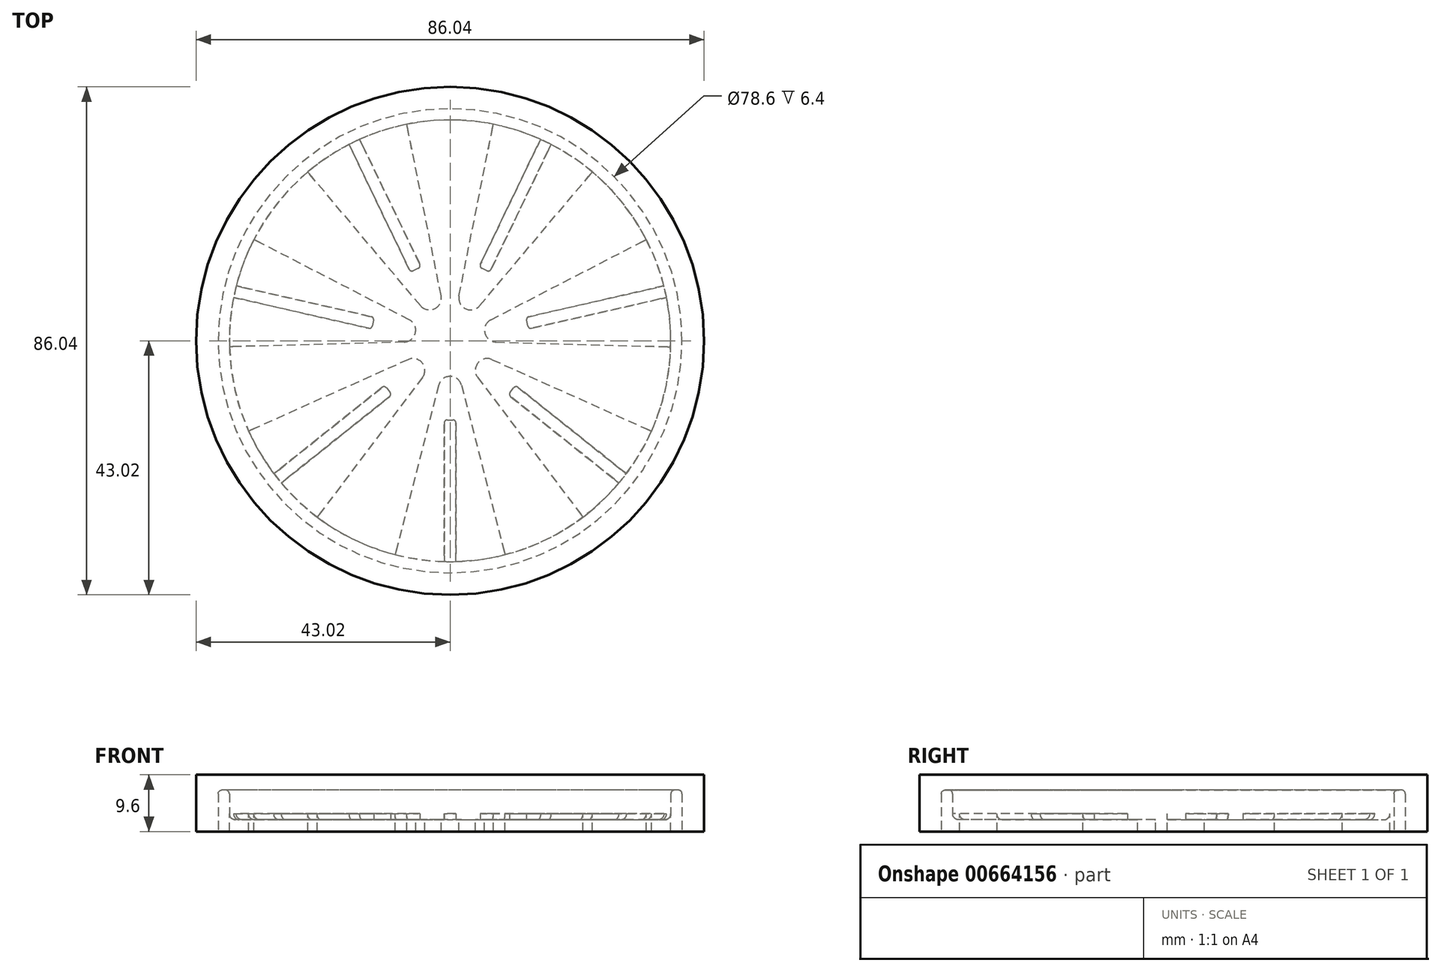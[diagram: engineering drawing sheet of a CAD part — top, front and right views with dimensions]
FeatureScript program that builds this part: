
annotation { "Feature Type Name" : "Feature", "Feature Type Description" : "" }
export const myFeature = defineFeature(function(context is Context, id is Id, definition is map)
    precondition{}
    {
        {
            var Q0;
            Q0=qCreatedBy(makeId("Top.planeOp"),FACE);
            var sketch = newSketch(context, id + "F0", { "sketchPlane" : qUnion([Q0])});
            skCircle(sketch, "E0", {"center": v(0, 0) * mm, "radius": 37.4 * mm});
            skCircle(sketch, "E1", {"center": v(0, 0) * mm, "radius": 39.3 * mm});
            skSolve(sketch);
        }
        {
            var Q0;
            Q0=makeQuery(id+"F0.imprint","IMPRINT",FACE,{"disambiguationData":[TD([[makeQuery(id+"F0.imprint","IMPRINT",EDGE,{"derivedFrom":sQuery(id+"F0.wireOp",EDGE,"E0")}),-1.0]])]});
            extrude(context, id + "F1", {"entities" : qUnion([Q0]), "depth" : 7 * mm, "offsetDistance" : 25 * mm});
        }
        {
            var Q0;
            Q0=qCreatedBy(makeId("Top.planeOp"),FACE);
            var sketch = newSketch(context, id + "F2", { "sketchPlane" : qUnion([Q0])});
            skCircle(sketch, "E2", {"center": v(0, 0) * mm, "radius": 37.45 * mm});
            skSolve(sketch);
        }
        {
            var Q0;
            Q0=makeQuery(id+"F2.imprint","IMPRINT",FACE,{"disambiguationData":[TD([[makeQuery(id+"F2.imprint","IMPRINT",EDGE,{"derivedFrom":sQuery(id+"F2.wireOp",EDGE,"E2")}),1.0]])]});
            extrude(context, id + "F3", {"entities" : qUnion([Q0]), "operationType" : NewBodyOperationType.ADD, "depth" : 2 * mm, "offsetDistance" : 25 * mm});
        }
        {
            var Q0;
            Q0=makeQuery(id+"F3.opExtrude","CAP_FACE",FACE,{"disambiguationData":[OSD([sQuery(id+"F2.wireOp",EDGE,"E2")])],"isStart":false});
            var sketch = newSketch(context, id + "F4", { "sketchPlane" : qUnion([Q0])});
            skCircle(sketch, "E3", {"center": v(0, 0) * mm, "radius": 38.06 * mm});
            skLineSegment(sketch, "E4", {"start": v(1.94, -7.53) * mm, "end": v(9.48, -36.86) * mm});
            skLineSegment(sketch, "E5.MirrorCS", {"start": v(-1.94, -7.53) * mm, "end": v(-9.48, -36.86) * mm});
            skPoint(sketch, "E6.orphan", {"position": v(-11.58, -45.02) * mm});
            skPoint(sketch, "E7.orphan", {"position": v(11.58, -45.02) * mm});
            skArc(sketch, "E8.filletArc", {"start": v(1.94, -7.53) * mm, "mid": v(0, -6.03) * mm, "end": v(-1.94, -7.53) * mm});
            skLineSegment(sketch, "E9.1.0", {"start": v(4.68, -6.21) * mm, "end": v(22.91, -30.4) * mm});
            skLineSegment(sketch, "E9.1.1", {"start": v(7.1, -3.18) * mm, "end": v(34.73, -15.57) * mm});
            skArc(sketch, "E9.1.2", {"start": v(7.1, -3.18) * mm, "mid": v(4.71, -3.76) * mm, "end": v(4.68, -6.21) * mm});
            skLineSegment(sketch, "E9.2.0", {"start": v(7.77, -0.21) * mm, "end": v(38.05, -1.04) * mm});
            skLineSegment(sketch, "E9.2.1", {"start": v(6.91, 3.56) * mm, "end": v(33.83, 17.45) * mm});
            skArc(sketch, "E9.2.2", {"start": v(6.91, 3.56) * mm, "mid": v(5.88, 1.34) * mm, "end": v(7.77, -0.21) * mm});
            skLineSegment(sketch, "E9.3.0", {"start": v(5.01, 5.95) * mm, "end": v(24.54, 29.1) * mm});
            skLineSegment(sketch, "E9.3.1", {"start": v(1.52, 7.63) * mm, "end": v(7.45, 37.33) * mm});
            skArc(sketch, "E9.3.2", {"start": v(1.52, 7.63) * mm, "mid": v(2.62, 5.43) * mm, "end": v(5.01, 5.95) * mm});
            skLineSegment(sketch, "E9.4.0", {"start": v(-1.52, 7.63) * mm, "end": v(-7.45, 37.33) * mm});
            skLineSegment(sketch, "E9.4.1", {"start": v(-5.01, 5.95) * mm, "end": v(-24.54, 29.1) * mm});
            skArc(sketch, "E9.4.2", {"start": v(-5.01, 5.95) * mm, "mid": v(-2.62, 5.43) * mm, "end": v(-1.52, 7.63) * mm});
            skLineSegment(sketch, "E9.5.0", {"start": v(-6.91, 3.56) * mm, "end": v(-33.83, 17.45) * mm});
            skLineSegment(sketch, "E9.5.1", {"start": v(-7.77, -0.21) * mm, "end": v(-38.05, -1.04) * mm});
            skArc(sketch, "E9.5.2", {"start": v(-7.77, -0.21) * mm, "mid": v(-5.88, 1.34) * mm, "end": v(-6.91, 3.56) * mm});
            skLineSegment(sketch, "E10.2.6.0", {"start": v(-7.1, -3.18) * mm, "end": v(-34.73, -15.57) * mm});
            skLineSegment(sketch, "E10.3.6.0", {"start": v(-4.68, -6.21) * mm, "end": v(-22.91, -30.4) * mm});
            skArc(sketch, "E10.6.6.0", {"start": v(-4.68, -6.21) * mm, "mid": v(-4.71, -3.76) * mm, "end": v(-7.1, -3.18) * mm});
            skSolve(sketch);
        }
        {
            var Q0;
            {var subQ24=sQuery(id+"F4.wireOp",EDGE,"E8.filletArc");Q0=makeQuery(id+"F4.imprint","IMPRINT",FACE,{"disambiguationData":[TD([[makeQuery(id+"F4.imprint","IMPRINT",EDGE,{"derivedFrom":subQ24}),-1.0]])]});}
            extrude(context, id + "F5", {"entities" : qUnion([Q0]), "operationType" : NewBodyOperationType.REMOVE, "oppositeDirection" : true, "depth" : 25 * mm, "offsetDistance" : 25 * mm});
        }
        {
            var Q0;
            Q0=makeQuery(id+"F3.boolean.opBoolean","MERGE",FACE,{"derivedFrom":[makeQuery(id+"F1.opExtrude","CAP_FACE",FACE,{"disambiguationData":[OSD([sQuery(id+"F0.wireOp",EDGE,"E0"),sQuery(id+"F0.wireOp",EDGE,"E1")])],"isStart":true}),makeQuery(id+"F3.opExtrude","CAP_FACE",FACE,{"disambiguationData":[OSD([sQuery(id+"F2.wireOp",EDGE,"E2")])],"isStart":true})]});
            var sketch = newSketch(context, id + "F6", { "sketchPlane" : qUnion([Q0])});
            skLineSegment(sketch, "E11", {"start": v(1, 38.32) * mm, "end": v(1, 13.9) * mm});
            skLineSegment(sketch, "E12", {"start": v(0.5, 13.4) * mm, "end": v(-0.5, 13.4) * mm});
            skLineSegment(sketch, "E13", {"start": v(-1, 13.9) * mm, "end": v(-1, 38.32) * mm});
            skPoint(sketch, "E14.visualSharp", {"position": v(-1, 13.4) * mm});
            skArc(sketch, "E14.filletArc", {"start": v(-1, 13.9) * mm, "mid": v(-0.85, 13.55) * mm, "end": v(-0.5, 13.4) * mm});
            skPoint(sketch, "E15.visualSharp", {"position": v(1, 13.4) * mm});
            skArc(sketch, "E15.filletArc", {"start": v(0.5, 13.4) * mm, "mid": v(0.85, 13.55) * mm, "end": v(1, 13.9) * mm});
            skLineSegment(sketch, "E16", {"start": v(-0.5, 38.82) * mm, "end": v(0.5, 38.82) * mm});
            skPoint(sketch, "E17.visualSharp", {"position": v(-1, 38.82) * mm});
            skArc(sketch, "E17.filletArc", {"start": v(-0.5, 38.82) * mm, "mid": v(-0.85, 38.68) * mm, "end": v(-1, 38.32) * mm});
            skPoint(sketch, "E18.visualSharp", {"position": v(1, 38.82) * mm});
            skArc(sketch, "E18.filletArc", {"start": v(1, 38.32) * mm, "mid": v(0.85, 38.68) * mm, "end": v(0.5, 38.82) * mm});
            skPoint(sketch, "E19.1.0", {"position": v(-11.1, 7.58) * mm});
            skPoint(sketch, "E19.1.1", {"position": v(-29.73, 24.99) * mm});
            skLineSegment(sketch, "E19.1.2", {"start": v(-11.5, 7.89) * mm, "end": v(-30.59, 23.11) * mm});
            skPoint(sketch, "E19.1.3", {"position": v(-30.98, 23.42) * mm});
            skLineSegment(sketch, "E19.1.4", {"start": v(-29.34, 24.68) * mm, "end": v(-10.25, 9.45) * mm});
            skPoint(sketch, "E19.1.5", {"position": v(-9.86, 9.14) * mm});
            skArc(sketch, "E19.1.6", {"start": v(-10.17, 8.75) * mm, "mid": v(-10.07, 9.12) * mm, "end": v(-10.25, 9.45) * mm});
            skArc(sketch, "E19.1.7", {"start": v(-30.66, 23.81) * mm, "mid": v(-30.77, 23.45) * mm, "end": v(-30.59, 23.11) * mm});
            skArc(sketch, "E19.1.8", {"start": v(-11.5, 7.89) * mm, "mid": v(-11.13, 7.78) * mm, "end": v(-10.8, 7.97) * mm});
            skLineSegment(sketch, "E19.1.9", {"start": v(-10.17, 8.75) * mm, "end": v(-10.8, 7.97) * mm});
            skLineSegment(sketch, "E19.1.10", {"start": v(-30.66, 23.81) * mm, "end": v(-30.04, 24.6) * mm});
            skArc(sketch, "E19.1.11", {"start": v(-29.34, 24.68) * mm, "mid": v(-29.7, 24.78) * mm, "end": v(-30.04, 24.6) * mm});
            skPoint(sketch, "E19.2.0", {"position": v(-12.85, -3.96) * mm});
            skPoint(sketch, "E19.2.1", {"position": v(-38.07, -7.66) * mm});
            skLineSegment(sketch, "E19.2.2", {"start": v(-13.34, -4.07) * mm, "end": v(-37.14, -9.5) * mm});
            skPoint(sketch, "E19.2.3", {"position": v(-37.63, -9.61) * mm});
            skLineSegment(sketch, "E19.2.4", {"start": v(-37.58, -7.55) * mm, "end": v(-13.78, -2.12) * mm});
            skPoint(sketch, "E19.2.5", {"position": v(-13.3, -2) * mm});
            skArc(sketch, "E19.2.6", {"start": v(-13.18, -2.5) * mm, "mid": v(-13.4, -2.18) * mm, "end": v(-13.78, -2.12) * mm});
            skArc(sketch, "E19.2.7", {"start": v(-37.74, -9.13) * mm, "mid": v(-37.52, -9.44) * mm, "end": v(-37.14, -9.5) * mm});
            skArc(sketch, "E19.2.8", {"start": v(-13.34, -4.07) * mm, "mid": v(-13.03, -3.85) * mm, "end": v(-12.96, -3.47) * mm});
            skLineSegment(sketch, "E19.2.9", {"start": v(-13.18, -2.5) * mm, "end": v(-12.96, -3.47) * mm});
            skLineSegment(sketch, "E19.2.10", {"start": v(-37.74, -9.13) * mm, "end": v(-37.96, -8.15) * mm});
            skArc(sketch, "E19.2.11", {"start": v(-37.58, -7.55) * mm, "mid": v(-37.9, -7.77) * mm, "end": v(-37.96, -8.15) * mm});
            skPoint(sketch, "E19.3.0", {"position": v(-4.92, -12.51) * mm});
            skPoint(sketch, "E19.3.1", {"position": v(-17.75, -34.54) * mm});
            skLineSegment(sketch, "E19.3.2", {"start": v(-5.13, -12.96) * mm, "end": v(-15.73, -34.96) * mm});
            skPoint(sketch, "E19.3.3", {"position": v(-15.94, -35.41) * mm});
            skLineSegment(sketch, "E19.3.4", {"start": v(-17.53, -34.1) * mm, "end": v(-6.94, -12.1) * mm});
            skPoint(sketch, "E19.3.5", {"position": v(-6.72, -11.65) * mm});
            skArc(sketch, "E19.3.6", {"start": v(-6.27, -11.86) * mm, "mid": v(-6.65, -11.84) * mm, "end": v(-6.94, -12.1) * mm});
            skArc(sketch, "E19.3.7", {"start": v(-16.4, -35.2) * mm, "mid": v(-16.01, -35.22) * mm, "end": v(-15.73, -34.96) * mm});
            skArc(sketch, "E19.3.8", {"start": v(-5.13, -12.96) * mm, "mid": v(-5.11, -12.58) * mm, "end": v(-5.37, -12.3) * mm});
            skLineSegment(sketch, "E19.3.9", {"start": v(-6.27, -11.86) * mm, "end": v(-5.37, -12.3) * mm});
            skLineSegment(sketch, "E19.3.10", {"start": v(-16.4, -35.2) * mm, "end": v(-17.3, -34.76) * mm});
            skArc(sketch, "E19.3.11", {"start": v(-17.53, -34.1) * mm, "mid": v(-17.55, -34.48) * mm, "end": v(-17.3, -34.76) * mm});
            skPoint(sketch, "E19.4.0", {"position": v(6.72, -11.65) * mm});
            skPoint(sketch, "E19.4.1", {"position": v(15.94, -35.41) * mm});
            skLineSegment(sketch, "E19.4.2", {"start": v(6.94, -12.1) * mm, "end": v(17.53, -34.1) * mm});
            skPoint(sketch, "E19.4.3", {"position": v(17.75, -34.54) * mm});
            skLineSegment(sketch, "E19.4.4", {"start": v(15.73, -34.96) * mm, "end": v(5.13, -12.96) * mm});
            skPoint(sketch, "E19.4.5", {"position": v(4.92, -12.51) * mm});
            skArc(sketch, "E19.4.6", {"start": v(5.37, -12.3) * mm, "mid": v(5.11, -12.58) * mm, "end": v(5.13, -12.96) * mm});
            skArc(sketch, "E19.4.7", {"start": v(17.3, -34.76) * mm, "mid": v(17.55, -34.48) * mm, "end": v(17.53, -34.1) * mm});
            skArc(sketch, "E19.4.8", {"start": v(6.94, -12.1) * mm, "mid": v(6.65, -11.84) * mm, "end": v(6.27, -11.86) * mm});
            skLineSegment(sketch, "E19.4.9", {"start": v(5.37, -12.3) * mm, "end": v(6.27, -11.86) * mm});
            skLineSegment(sketch, "E19.4.10", {"start": v(17.3, -34.76) * mm, "end": v(16.4, -35.2) * mm});
            skArc(sketch, "E19.4.11", {"start": v(15.73, -34.96) * mm, "mid": v(16.01, -35.22) * mm, "end": v(16.4, -35.2) * mm});
            skPoint(sketch, "E19.5.0", {"position": v(13.3, -2) * mm});
            skPoint(sketch, "E19.5.1", {"position": v(37.63, -9.61) * mm});
            skLineSegment(sketch, "E19.5.2", {"start": v(13.78, -2.12) * mm, "end": v(37.58, -7.55) * mm});
            skPoint(sketch, "E19.5.3", {"position": v(38.07, -7.66) * mm});
            skLineSegment(sketch, "E19.5.4", {"start": v(37.14, -9.5) * mm, "end": v(13.34, -4.07) * mm});
            skPoint(sketch, "E19.5.5", {"position": v(12.85, -3.96) * mm});
            skArc(sketch, "E19.5.6", {"start": v(12.96, -3.47) * mm, "mid": v(13.03, -3.85) * mm, "end": v(13.34, -4.07) * mm});
            skArc(sketch, "E19.5.7", {"start": v(37.96, -8.15) * mm, "mid": v(37.9, -7.77) * mm, "end": v(37.58, -7.55) * mm});
            skArc(sketch, "E19.5.8", {"start": v(13.78, -2.12) * mm, "mid": v(13.4, -2.18) * mm, "end": v(13.18, -2.5) * mm});
            skLineSegment(sketch, "E19.5.9", {"start": v(12.96, -3.47) * mm, "end": v(13.18, -2.5) * mm});
            skLineSegment(sketch, "E19.5.10", {"start": v(37.96, -8.15) * mm, "end": v(37.74, -9.13) * mm});
            skArc(sketch, "E19.5.11", {"start": v(37.14, -9.5) * mm, "mid": v(37.52, -9.44) * mm, "end": v(37.74, -9.13) * mm});
            skPoint(sketch, "E19.6.0", {"position": v(9.86, 9.14) * mm});
            skPoint(sketch, "E19.6.1", {"position": v(30.98, 23.42) * mm});
            skLineSegment(sketch, "E19.6.2", {"start": v(10.25, 9.45) * mm, "end": v(29.34, 24.68) * mm});
            skPoint(sketch, "E19.6.3", {"position": v(29.73, 24.99) * mm});
            skLineSegment(sketch, "E19.6.4", {"start": v(30.59, 23.11) * mm, "end": v(11.5, 7.89) * mm});
            skPoint(sketch, "E19.6.5", {"position": v(11.1, 7.58) * mm});
            skArc(sketch, "E19.6.6", {"start": v(10.8, 7.97) * mm, "mid": v(11.13, 7.78) * mm, "end": v(11.5, 7.89) * mm});
            skArc(sketch, "E19.6.7", {"start": v(30.04, 24.6) * mm, "mid": v(29.7, 24.78) * mm, "end": v(29.34, 24.68) * mm});
            skArc(sketch, "E19.6.8", {"start": v(10.25, 9.45) * mm, "mid": v(10.07, 9.12) * mm, "end": v(10.17, 8.75) * mm});
            skLineSegment(sketch, "E19.6.9", {"start": v(10.8, 7.97) * mm, "end": v(10.17, 8.75) * mm});
            skLineSegment(sketch, "E19.6.10", {"start": v(30.04, 24.6) * mm, "end": v(30.66, 23.81) * mm});
            skArc(sketch, "E19.6.11", {"start": v(30.59, 23.11) * mm, "mid": v(30.77, 23.45) * mm, "end": v(30.66, 23.81) * mm});
            skPoint(sketch, "E19.center", {"position": v(0, 0) * mm});
            skSolve(sketch);
        }
        {
            var Q0;
            Q0=qSketchRegion(id+"F6",true);
            extrude(context, id + "F7", {"entities" : qUnion([Q0]), "operationType" : NewBodyOperationType.ADD, "depth" : -3 * mm, "offsetDistance" : 25 * mm});
        }
        {
            var Q0;
            {var subQ0=sQuery(id+"F2.wireOp",EDGE,"E2");var subQ1=makeQuery(id+"F3.opExtrude","CAP_FACE",FACE,{"disambiguationData":[OSD([subQ0])],"isStart":false});var subQ2=sQuery(id+"F0.wireOp",EDGE,"E0");var subQ3=makeQuery(id+"F1.opExtrude","SWEPT_FACE",FACE,{"disambiguationData":[OSD([subQ2])]});var subQ4=makeQuery(id+"F3.boolean.opBoolean","INTERSECT",EDGE,{"derivedFrom":[subQ3,subQ1]});var subQ5=sQuery(id+"F4.wireOp",EDGE,"E10.2.6.0");var subQ8=makeQuery(id+"F5.opExtrude","SWEPT_FACE",FACE,{"disambiguationData":[OSD([subQ5])]});Q0=makeQuery(id+"F7.boolean.opBoolean","SPLIT",EDGE,{"disambiguationData":[TD([makeQuery(id+"F5.boolean.opBoolean","COPY",FACE,{"derivedFrom":subQ8})])],"derivedFrom":makeQuery(id+"F5.boolean.opBoolean","SPLIT",EDGE,{"disambiguationData":[TD([subQ8])],"derivedFrom":subQ4})});}
            var Q1;
            {var subQ0=sQuery(id+"F2.wireOp",EDGE,"E2");var subQ1=makeQuery(id+"F3.opExtrude","CAP_FACE",FACE,{"disambiguationData":[OSD([subQ0])],"isStart":false});var subQ2=sQuery(id+"F0.wireOp",EDGE,"E0");var subQ3=makeQuery(id+"F1.opExtrude","SWEPT_FACE",FACE,{"disambiguationData":[OSD([subQ2])]});var subQ4=makeQuery(id+"F3.boolean.opBoolean","INTERSECT",EDGE,{"derivedFrom":[subQ3,subQ1]});var subQ6=sQuery(id+"F4.wireOp",EDGE,"E5.MirrorCS");var subQ7=makeQuery(id+"F5.opExtrude","SWEPT_FACE",FACE,{"disambiguationData":[OSD([subQ6])]});var subQ12=sQuery(id+"F4.wireOp",EDGE,"E4");Q1=makeQuery(id+"F7.boolean.opBoolean","SPLIT",EDGE,{"disambiguationData":[TD([makeQuery(id+"F5.boolean.opBoolean","COPY",FACE,{"derivedFrom":subQ7})])],"derivedFrom":makeQuery(id+"F5.boolean.opBoolean","SPLIT",EDGE,{"disambiguationData":[TD([makeQuery(id+"F5.opExtrude","SWEPT_FACE",FACE,{"disambiguationData":[OSD([subQ12])]})])],"derivedFrom":subQ4})});}
            var Q2;
            {var subQ0=sQuery(id+"F2.wireOp",EDGE,"E2");var subQ1=makeQuery(id+"F3.opExtrude","CAP_FACE",FACE,{"disambiguationData":[OSD([subQ0])],"isStart":false});var subQ2=sQuery(id+"F0.wireOp",EDGE,"E0");var subQ3=makeQuery(id+"F1.opExtrude","SWEPT_FACE",FACE,{"disambiguationData":[OSD([subQ2])]});var subQ4=makeQuery(id+"F3.boolean.opBoolean","INTERSECT",EDGE,{"derivedFrom":[subQ3,subQ1]});var subQ9=sQuery(id+"F4.wireOp",EDGE,"E4");var subQ10=makeQuery(id+"F5.opExtrude","SWEPT_FACE",FACE,{"disambiguationData":[OSD([subQ9])]});Q2=makeQuery(id+"F7.boolean.opBoolean","SPLIT",EDGE,{"disambiguationData":[TD([makeQuery(id+"F5.boolean.opBoolean","COPY",FACE,{"derivedFrom":subQ10})])],"derivedFrom":makeQuery(id+"F5.boolean.opBoolean","SPLIT",EDGE,{"disambiguationData":[TD([subQ10])],"derivedFrom":subQ4})});}
            var Q3;
            {var subQ0=sQuery(id+"F2.wireOp",EDGE,"E2");var subQ1=makeQuery(id+"F3.opExtrude","CAP_FACE",FACE,{"disambiguationData":[OSD([subQ0])],"isStart":false});var subQ2=sQuery(id+"F0.wireOp",EDGE,"E0");var subQ3=makeQuery(id+"F1.opExtrude","SWEPT_FACE",FACE,{"disambiguationData":[OSD([subQ2])]});var subQ4=makeQuery(id+"F3.boolean.opBoolean","INTERSECT",EDGE,{"derivedFrom":[subQ3,subQ1]});var subQ5=sQuery(id+"F4.wireOp",EDGE,"E10.2.6.0");var subQ7=sQuery(id+"F4.wireOp",EDGE,"E10.3.6.0");var subQ8=makeQuery(id+"F5.opExtrude","SWEPT_FACE",FACE,{"disambiguationData":[OSD([subQ7])]});Q3=makeQuery(id+"F7.boolean.opBoolean","SPLIT",EDGE,{"disambiguationData":[TD([makeQuery(id+"F5.boolean.opBoolean","COPY",FACE,{"derivedFrom":subQ8})])],"derivedFrom":makeQuery(id+"F5.boolean.opBoolean","SPLIT",EDGE,{"disambiguationData":[TD([makeQuery(id+"F5.opExtrude","SWEPT_FACE",FACE,{"disambiguationData":[OSD([subQ5])]})])],"derivedFrom":subQ4})});}
            var Q4;
            {var subQ0=sQuery(id+"F2.wireOp",EDGE,"E2");var subQ1=makeQuery(id+"F3.opExtrude","CAP_FACE",FACE,{"disambiguationData":[OSD([subQ0])],"isStart":false});var subQ2=sQuery(id+"F0.wireOp",EDGE,"E0");var subQ3=makeQuery(id+"F1.opExtrude","SWEPT_FACE",FACE,{"disambiguationData":[OSD([subQ2])]});var subQ4=makeQuery(id+"F3.boolean.opBoolean","INTERSECT",EDGE,{"derivedFrom":[subQ3,subQ1]});var subQ11=sQuery(id+"F4.wireOp",EDGE,"E9.1.0");var subQ12=makeQuery(id+"F5.opExtrude","SWEPT_FACE",FACE,{"disambiguationData":[OSD([subQ11])]});Q4=makeQuery(id+"F7.boolean.opBoolean","SPLIT",EDGE,{"disambiguationData":[TD([makeQuery(id+"F5.boolean.opBoolean","COPY",FACE,{"derivedFrom":subQ12})])],"derivedFrom":makeQuery(id+"F5.boolean.opBoolean","SPLIT",EDGE,{"disambiguationData":[TD([subQ12])],"derivedFrom":subQ4})});}
            var Q5;
            {var subQ0=sQuery(id+"F4.wireOp",EDGE,"E9.1.1");var subQ1=makeQuery(id+"F5.opExtrude","SWEPT_FACE",FACE,{"disambiguationData":[OSD([subQ0])]});var subQ2=sQuery(id+"F2.wireOp",EDGE,"E2");var subQ3=makeQuery(id+"F3.opExtrude","CAP_FACE",FACE,{"disambiguationData":[OSD([subQ2])],"isStart":false});var subQ4=sQuery(id+"F0.wireOp",EDGE,"E0");var subQ5=makeQuery(id+"F1.opExtrude","SWEPT_FACE",FACE,{"disambiguationData":[OSD([subQ4])]});var subQ6=makeQuery(id+"F3.boolean.opBoolean","INTERSECT",EDGE,{"derivedFrom":[subQ5,subQ3]});var subQ12=sQuery(id+"F4.wireOp",EDGE,"E9.1.0");Q5=makeQuery(id+"F7.boolean.opBoolean","SPLIT",EDGE,{"disambiguationData":[TD([makeQuery(id+"F5.boolean.opBoolean","COPY",FACE,{"derivedFrom":subQ1})])],"derivedFrom":makeQuery(id+"F5.boolean.opBoolean","SPLIT",EDGE,{"disambiguationData":[TD([makeQuery(id+"F5.opExtrude","SWEPT_FACE",FACE,{"disambiguationData":[OSD([subQ12])]})])],"derivedFrom":subQ6})});}
            var Q6;
            {var subQ0=sQuery(id+"F4.wireOp",EDGE,"E9.5.0");var subQ1=makeQuery(id+"F5.opExtrude","SWEPT_FACE",FACE,{"disambiguationData":[OSD([subQ0])]});var subQ2=sQuery(id+"F2.wireOp",EDGE,"E2");var subQ3=makeQuery(id+"F3.opExtrude","CAP_FACE",FACE,{"disambiguationData":[OSD([subQ2])],"isStart":false});var subQ4=sQuery(id+"F0.wireOp",EDGE,"E0");var subQ5=makeQuery(id+"F1.opExtrude","SWEPT_FACE",FACE,{"disambiguationData":[OSD([subQ4])]});var subQ6=makeQuery(id+"F3.boolean.opBoolean","INTERSECT",EDGE,{"derivedFrom":[subQ5,subQ3]});Q6=makeQuery(id+"F7.boolean.opBoolean","SPLIT",EDGE,{"disambiguationData":[TD([makeQuery(id+"F5.boolean.opBoolean","COPY",FACE,{"derivedFrom":subQ1})])],"derivedFrom":makeQuery(id+"F5.boolean.opBoolean","SPLIT",EDGE,{"disambiguationData":[TD([subQ1])],"derivedFrom":subQ6})});}
            var Q7;
            {var subQ0=sQuery(id+"F4.wireOp",EDGE,"E9.4.1");var subQ1=makeQuery(id+"F5.opExtrude","SWEPT_FACE",FACE,{"disambiguationData":[OSD([subQ0])]});var subQ2=sQuery(id+"F2.wireOp",EDGE,"E2");var subQ3=makeQuery(id+"F3.opExtrude","CAP_FACE",FACE,{"disambiguationData":[OSD([subQ2])],"isStart":false});var subQ4=sQuery(id+"F0.wireOp",EDGE,"E0");var subQ5=makeQuery(id+"F1.opExtrude","SWEPT_FACE",FACE,{"disambiguationData":[OSD([subQ4])]});var subQ6=makeQuery(id+"F3.boolean.opBoolean","INTERSECT",EDGE,{"derivedFrom":[subQ5,subQ3]});var subQ12=sQuery(id+"F4.wireOp",EDGE,"E9.4.0");Q7=makeQuery(id+"F7.boolean.opBoolean","SPLIT",EDGE,{"disambiguationData":[TD([makeQuery(id+"F5.boolean.opBoolean","COPY",FACE,{"derivedFrom":subQ1})])],"derivedFrom":makeQuery(id+"F5.boolean.opBoolean","SPLIT",EDGE,{"disambiguationData":[TD([makeQuery(id+"F5.opExtrude","SWEPT_FACE",FACE,{"disambiguationData":[OSD([subQ12])]})])],"derivedFrom":subQ6})});}
            var Q8;
            {var subQ0=sQuery(id+"F2.wireOp",EDGE,"E2");var subQ1=makeQuery(id+"F3.opExtrude","CAP_FACE",FACE,{"disambiguationData":[OSD([subQ0])],"isStart":false});var subQ2=sQuery(id+"F0.wireOp",EDGE,"E0");var subQ3=makeQuery(id+"F1.opExtrude","SWEPT_FACE",FACE,{"disambiguationData":[OSD([subQ2])]});var subQ4=makeQuery(id+"F3.boolean.opBoolean","INTERSECT",EDGE,{"derivedFrom":[subQ3,subQ1]});var subQ6=sQuery(id+"F4.wireOp",EDGE,"E9.4.0");var subQ7=makeQuery(id+"F5.opExtrude","SWEPT_FACE",FACE,{"disambiguationData":[OSD([subQ6])]});Q8=makeQuery(id+"F7.boolean.opBoolean","SPLIT",EDGE,{"disambiguationData":[TD([makeQuery(id+"F5.boolean.opBoolean","COPY",FACE,{"derivedFrom":subQ7})])],"derivedFrom":makeQuery(id+"F5.boolean.opBoolean","SPLIT",EDGE,{"disambiguationData":[TD([subQ7])],"derivedFrom":subQ4})});}
            var Q9;
            {var subQ0=sQuery(id+"F4.wireOp",EDGE,"E9.5.1");var subQ1=makeQuery(id+"F5.opExtrude","SWEPT_FACE",FACE,{"disambiguationData":[OSD([subQ0])]});var subQ2=sQuery(id+"F2.wireOp",EDGE,"E2");var subQ3=makeQuery(id+"F3.opExtrude","CAP_FACE",FACE,{"disambiguationData":[OSD([subQ2])],"isStart":false});var subQ4=sQuery(id+"F0.wireOp",EDGE,"E0");var subQ5=makeQuery(id+"F1.opExtrude","SWEPT_FACE",FACE,{"disambiguationData":[OSD([subQ4])]});var subQ6=makeQuery(id+"F3.boolean.opBoolean","INTERSECT",EDGE,{"derivedFrom":[subQ5,subQ3]});var subQ9=sQuery(id+"F4.wireOp",EDGE,"E9.5.0");Q9=makeQuery(id+"F7.boolean.opBoolean","SPLIT",EDGE,{"disambiguationData":[TD([makeQuery(id+"F5.boolean.opBoolean","COPY",FACE,{"derivedFrom":subQ1})])],"derivedFrom":makeQuery(id+"F5.boolean.opBoolean","SPLIT",EDGE,{"disambiguationData":[TD([makeQuery(id+"F5.opExtrude","SWEPT_FACE",FACE,{"disambiguationData":[OSD([subQ9])]})])],"derivedFrom":subQ6})});}
            var Q10;
            {var subQ0=sQuery(id+"F4.wireOp",EDGE,"E9.2.0");var subQ1=makeQuery(id+"F5.opExtrude","SWEPT_FACE",FACE,{"disambiguationData":[OSD([subQ0])]});var subQ2=sQuery(id+"F2.wireOp",EDGE,"E2");var subQ3=makeQuery(id+"F3.opExtrude","CAP_FACE",FACE,{"disambiguationData":[OSD([subQ2])],"isStart":false});var subQ4=sQuery(id+"F0.wireOp",EDGE,"E0");var subQ5=makeQuery(id+"F1.opExtrude","SWEPT_FACE",FACE,{"disambiguationData":[OSD([subQ4])]});var subQ6=makeQuery(id+"F3.boolean.opBoolean","INTERSECT",EDGE,{"derivedFrom":[subQ5,subQ3]});Q10=makeQuery(id+"F7.boolean.opBoolean","SPLIT",EDGE,{"disambiguationData":[TD([makeQuery(id+"F5.boolean.opBoolean","COPY",FACE,{"derivedFrom":subQ1})])],"derivedFrom":makeQuery(id+"F5.boolean.opBoolean","SPLIT",EDGE,{"disambiguationData":[TD([subQ1])],"derivedFrom":subQ6})});}
            var Q11;
            {var subQ0=sQuery(id+"F2.wireOp",EDGE,"E2");var subQ1=makeQuery(id+"F3.opExtrude","CAP_FACE",FACE,{"disambiguationData":[OSD([subQ0])],"isStart":false});var subQ2=sQuery(id+"F0.wireOp",EDGE,"E0");var subQ3=makeQuery(id+"F1.opExtrude","SWEPT_FACE",FACE,{"disambiguationData":[OSD([subQ2])]});var subQ4=makeQuery(id+"F3.boolean.opBoolean","INTERSECT",EDGE,{"derivedFrom":[subQ3,subQ1]});var subQ7=sQuery(id+"F4.wireOp",EDGE,"E9.2.1");var subQ9=sQuery(id+"F4.wireOp",EDGE,"E9.2.0");var subQ12=makeQuery(id+"F5.opExtrude","SWEPT_FACE",FACE,{"disambiguationData":[OSD([subQ7])]});Q11=makeQuery(id+"F7.boolean.opBoolean","SPLIT",EDGE,{"disambiguationData":[TD([makeQuery(id+"F5.boolean.opBoolean","COPY",FACE,{"derivedFrom":subQ12})])],"derivedFrom":makeQuery(id+"F5.boolean.opBoolean","SPLIT",EDGE,{"disambiguationData":[TD([makeQuery(id+"F5.opExtrude","SWEPT_FACE",FACE,{"disambiguationData":[OSD([subQ9])]})])],"derivedFrom":subQ4})});}
            var Q12;
            {var subQ0=sQuery(id+"F2.wireOp",EDGE,"E2");var subQ1=makeQuery(id+"F3.opExtrude","CAP_FACE",FACE,{"disambiguationData":[OSD([subQ0])],"isStart":false});var subQ2=sQuery(id+"F0.wireOp",EDGE,"E0");var subQ3=makeQuery(id+"F1.opExtrude","SWEPT_FACE",FACE,{"disambiguationData":[OSD([subQ2])]});var subQ4=makeQuery(id+"F3.boolean.opBoolean","INTERSECT",EDGE,{"derivedFrom":[subQ3,subQ1]});var subQ7=sQuery(id+"F4.wireOp",EDGE,"E9.3.0");var subQ9=makeQuery(id+"F5.opExtrude","SWEPT_FACE",FACE,{"disambiguationData":[OSD([subQ7])]});Q12=makeQuery(id+"F7.boolean.opBoolean","SPLIT",EDGE,{"disambiguationData":[TD([makeQuery(id+"F5.boolean.opBoolean","COPY",FACE,{"derivedFrom":subQ9})])],"derivedFrom":makeQuery(id+"F5.boolean.opBoolean","SPLIT",EDGE,{"disambiguationData":[TD([subQ9])],"derivedFrom":subQ4})});}
            var Q13;
            {var subQ0=sQuery(id+"F2.wireOp",EDGE,"E2");var subQ1=makeQuery(id+"F3.opExtrude","CAP_FACE",FACE,{"disambiguationData":[OSD([subQ0])],"isStart":false});var subQ2=sQuery(id+"F0.wireOp",EDGE,"E0");var subQ3=makeQuery(id+"F1.opExtrude","SWEPT_FACE",FACE,{"disambiguationData":[OSD([subQ2])]});var subQ4=makeQuery(id+"F3.boolean.opBoolean","INTERSECT",EDGE,{"derivedFrom":[subQ3,subQ1]});var subQ7=sQuery(id+"F4.wireOp",EDGE,"E9.3.1");var subQ8=makeQuery(id+"F5.opExtrude","SWEPT_FACE",FACE,{"disambiguationData":[OSD([subQ7])]});var subQ9=sQuery(id+"F4.wireOp",EDGE,"E9.3.0");Q13=makeQuery(id+"F7.boolean.opBoolean","SPLIT",EDGE,{"disambiguationData":[TD([makeQuery(id+"F5.boolean.opBoolean","COPY",FACE,{"derivedFrom":subQ8})])],"derivedFrom":makeQuery(id+"F5.boolean.opBoolean","SPLIT",EDGE,{"disambiguationData":[TD([makeQuery(id+"F5.opExtrude","SWEPT_FACE",FACE,{"disambiguationData":[OSD([subQ9])]})])],"derivedFrom":subQ4})});}
            fillet(context, id + "F8", {"entities" : qUnion([Q0, Q1, Q2, Q3, Q4, Q5, Q6, Q7, Q8, Q9, Q10, Q11, Q12, Q13]), "radius" : 1 * mm, "tangentPropagation" : true, "allowEdgeOverflow" : false});
        }
        {
            var Q0;
            Q0=makeQuery(id+"F1.opExtrude","CAP_EDGE",EDGE,{"disambiguationData":[OSD([sQuery(id+"F0.wireOp",EDGE,"E1")])],"isStart":false});
            var Q1;
            Q1=makeQuery(id+"F1.opExtrude","CAP_EDGE",EDGE,{"disambiguationData":[OSD([sQuery(id+"F0.wireOp",EDGE,"E0")])],"isStart":false});
            fillet(context, id + "F9", {"entities" : qUnion([Q0, Q1]), "radius" : 0.6 * mm, "tangentPropagation" : true, "allowEdgeOverflow" : false});
        }
        {
            var Q0;
            Q0=makeQuery(id+"F3.boolean.opBoolean","MERGE",FACE,{"derivedFrom":[makeQuery(id+"F1.opExtrude","CAP_FACE",FACE,{"disambiguationData":[OSD([sQuery(id+"F0.wireOp",EDGE,"E0"),sQuery(id+"F0.wireOp",EDGE,"E1")])],"isStart":true}),makeQuery(id+"F3.opExtrude","CAP_FACE",FACE,{"disambiguationData":[OSD([sQuery(id+"F2.wireOp",EDGE,"E2")])],"isStart":true})]});
            var sketch = newSketch(context, id + "F10", { "sketchPlane" : qUnion([Q0])});
            skCircle(sketch, "E20", {"center": v(0, 0) * mm, "radius": 43.02 * mm});
            skSolve(sketch);
        }
        {
            var Q0;
            Q0 = qSketchRegion(id + "F10", true);
            extrude(context, id + "F11", {"entities" : qUnion([Q0]), "oppositeDirection" : true, "depth" : 9.6 * mm, "offsetDistance" : 25 * mm});
        }
        {
            var Q0;
            Q0=makeQuery(id+"F1.opExtrude","SWEPT_BODY",BODY,{"disambiguationData":[OSD([sQuery(id+"F0.wireOp",EDGE,"E0"),sQuery(id+"F0.wireOp",EDGE,"E1")])]});
            var Q1;
            Q1=makeQuery(id+"F11.opExtrude","SWEPT_BODY",BODY,{"disambiguationData":[OSD([sQuery(id+"F10.wireOp",EDGE,"E20")])]});
            booleanBodies(context, id + "F12", {"operationType" : BooleanOperationType.SUBTRACTION, "tools" : qUnion([Q0]), "targets" : qUnion([Q1])});
        }
    });
